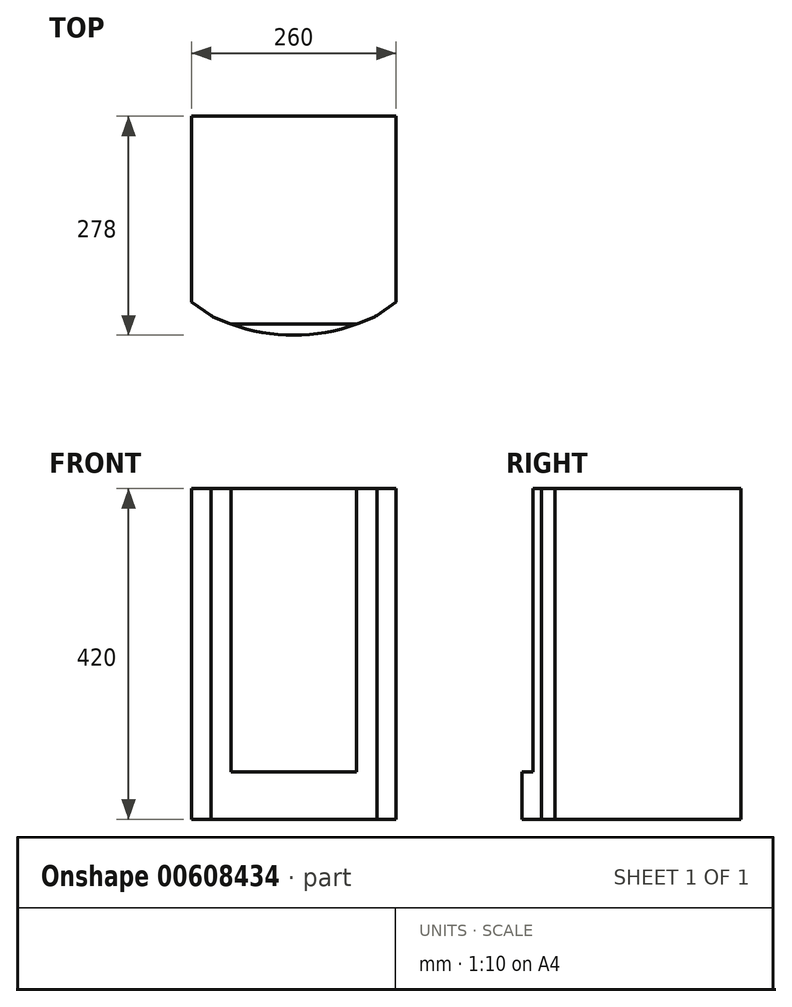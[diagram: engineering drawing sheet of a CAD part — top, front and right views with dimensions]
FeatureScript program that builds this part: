
annotation { "Feature Type Name" : "Feature", "Feature Type Description" : "" }
export const myFeature = defineFeature(function(context is Context, id is Id, definition is map)
    precondition{}
    {
        {
            var Q0;
            Q0=qCreatedBy(makeId("Front.planeOp"),FACE);
            var sketch = newSketch(context, id + "F0", { "sketchPlane" : qUnion([Q0])});
            skLineSegment(sketch, "E0.bottom", {"start": v(0, 0) * mm, "end": v(260, 0) * mm});
            skLineSegment(sketch, "E0.top", {"start": v(0, 420) * mm, "end": v(260, 420) * mm});
            skLineSegment(sketch, "E0.left", {"start": v(0, 0) * mm, "end": v(0, 420) * mm});
            skLineSegment(sketch, "E0.right", {"start": v(260, 0) * mm, "end": v(260, 420) * mm});
            skSolve(sketch);
        }
        {
            var Q0;
            Q0 = qSketchRegion(id + "F0", true);
            extrude(context, id + "F1", {"entities" : qUnion([Q0]), "depth" : 230 * mm, "offsetDistance" : 25 * mm});
        }
        {
            var Q0;
            Q0=qCreatedBy(makeId("Top.planeOp"),FACE);
            var sketch = newSketch(context, id + "F2", { "sketchPlane" : qUnion([Q0])});
            skLineSegment(sketch, "E1", {"start": v(0, -230) * mm, "end": v(260, -230) * mm});
            skLineSegment(sketch, "E2", {"start": v(260, -230) * mm, "end": v(260, -236) * mm});
            skLineSegment(sketch, "E3", {"start": v(0, -230) * mm, "end": v(0, -236) * mm});
            skLineSegment(sketch, "E4", {"start": v(0, -236) * mm, "end": v(24.57, -253.2) * mm});
            skLineSegment(sketch, "E5", {"start": v(260, -236) * mm, "end": v(235.43, -253.2) * mm});
            skArc(sketch, "E6", {"start": v(24.57, -253.2) * mm, "mid": v(130, -278) * mm, "end": v(235.43, -253.2) * mm});
            skSolve(sketch);
        }
        {
            var Q0;
            Q0 = qSketchRegion(id + "F2", true);
            var Q1;
            Q1=makeQuery(id+"F1.opExtrude","SWEPT_FACE",FACE,{"disambiguationData":[OSD([sQuery(id+"F0.wireOp",EDGE,"E0.top")])]});
            extrude(context, id + "F3", {"entities" : qUnion([Q0]), "operationType" : NewBodyOperationType.ADD, "endBound" : BoundingType.UP_TO_SURFACE, "depth" : 25 * mm, "endBoundEntityFace" : qUnion([Q1]), "offsetDistance" : 25 * mm});
        }
        {
            var Q0;
            {var subQ0=sQuery(id+"F0.wireOp",EDGE,"E0.top");Q0=makeQuery(id+"F3.boolean.opBoolean","MERGE",FACE,{"derivedFrom":[makeQuery(id+"F1.opExtrude","SWEPT_FACE",FACE,{"disambiguationData":[OSD([subQ0])]}),makeQuery(id+"F3.opExtrude","CAP_FACE",FACE,{"disambiguationData":[OSD([subQ0])],"isStart":false})]});}
            var sketch = newSketch(context, id + "F4", { "sketchPlane" : qUnion([Q0])});
            skLineSegment(sketch, "E7.bottom", {"start": v(210, -340.17) * mm, "end": v(50, -340.17) * mm});
            skLineSegment(sketch, "E7.top", {"start": v(210, -264.06) * mm, "end": v(50, -264.06) * mm});
            skLineSegment(sketch, "E7.left", {"start": v(210, -340.17) * mm, "end": v(210, -264.06) * mm});
            skLineSegment(sketch, "E7.right", {"start": v(50, -340.17) * mm, "end": v(50, -264.06) * mm});
            skSolve(sketch);
        }
        {
            var Q0;
            Q0 = qSketchRegion(id + "F4", true);
            extrude(context, id + "F5", {"entities" : qUnion([Q0]), "operationType" : NewBodyOperationType.REMOVE, "oppositeDirection" : true, "depth" : 360 * mm, "offsetDistance" : 25 * mm});
        }
    });
